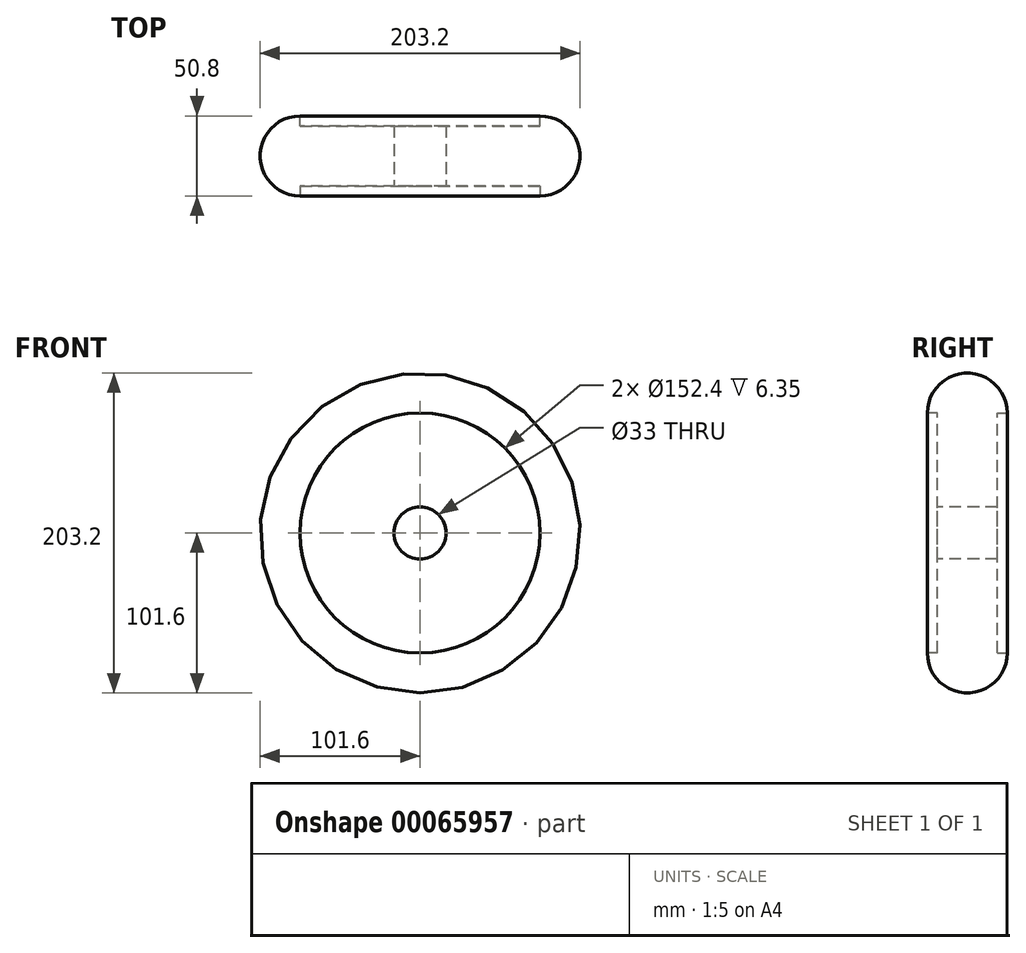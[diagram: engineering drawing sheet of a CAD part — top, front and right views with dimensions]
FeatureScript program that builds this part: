
annotation { "Feature Type Name" : "Feature", "Feature Type Description" : "" }
export const myFeature = defineFeature(function(context is Context, id is Id, definition is map)
    precondition{}
    {
        {
            var Q0;
            Q0=qCreatedBy(makeId("Front.planeOp"),FACE);
            var sketch = newSketch(context, id + "F0", { "sketchPlane" : qUnion([Q0])});
            skCircle(sketch, "E0", {"center": v(0, 0) * mm, "radius": 101.6 * mm});
            skSolve(sketch);
        }
        {
            var Q0;
            Q0=makeQuery(id+"F0.imprint","IMPRINT",FACE,{"disambiguationData":[TD([[makeQuery(id+"F0.imprint","IMPRINT",EDGE,{"derivedFrom":sQuery(id+"F0.wireOp",EDGE,"E0")}),1.0]])]});
            extrude(context, id + "F1", {"entities" : qUnion([Q0]), "depth" : 50.8 * mm});
        }
        {
            var Q0;
            Q0=makeQuery(id+"F1.opExtrude","CAP_EDGE",EDGE,{"disambiguationData":[OSD([sQuery(id+"F0.wireOp",EDGE,"E0")])],"isStart":false});
            var Q1;
            Q1=makeQuery(id+"F1.opExtrude","CAP_EDGE",EDGE,{"disambiguationData":[OSD([sQuery(id+"F0.wireOp",EDGE,"E0")])],"isStart":true});
            fillet(context, id + "F2", {"entities" : qUnion([Q0, Q1]), "radius" : 25.4 * mm, "tangentPropagation" : true, "allowEdgeOverflow" : false});
        }
        {
            var Q0;
            Q0=makeQuery(id+"F1.opExtrude","CAP_FACE",FACE,{"disambiguationData":[OSD([sQuery(id+"F0.wireOp",EDGE,"E0")])],"isStart":false});
            var sketch = newSketch(context, id + "F3", { "sketchPlane" : qUnion([Q0])});
            skCircle(sketch, "E1", {"center": v(0, 0) * mm, "radius": 16.5 * mm});
            skSolve(sketch);
        }
        {
            var Q0;
            Q0=makeQuery(id+"F3.imprint","IMPRINT",FACE,{"disambiguationData":[TD([[makeQuery(id+"F3.imprint","IMPRINT",EDGE,{"derivedFrom":sQuery(id+"F3.wireOp",EDGE,"E1")}),1.0]])]});
            extrude(context, id + "F4", {"entities" : qUnion([Q0]), "operationType" : NewBodyOperationType.REMOVE, "endBound" : BoundingType.THROUGH_ALL, "oppositeDirection" : true, "depth" : 25.4 * mm});
        }
        {
            var Q0;
            Q0=makeQuery(id+"F1.opExtrude","CAP_FACE",FACE,{"disambiguationData":[OSD([sQuery(id+"F0.wireOp",EDGE,"E0")])],"isStart":false});
            extrude(context, id + "F5", {"entities" : qUnion([Q0]), "operationType" : NewBodyOperationType.REMOVE, "oppositeDirection" : true, "depth" : 6.35 * mm});
        }
        {
            var Q0;
            Q0=makeQuery(id+"F1.opExtrude","CAP_FACE",FACE,{"disambiguationData":[OSD([sQuery(id+"F0.wireOp",EDGE,"E0")])],"isStart":true});
            extrude(context, id + "F6", {"entities" : qUnion([Q0]), "operationType" : NewBodyOperationType.REMOVE, "oppositeDirection" : true, "depth" : 6.35 * mm});
        }
    });
